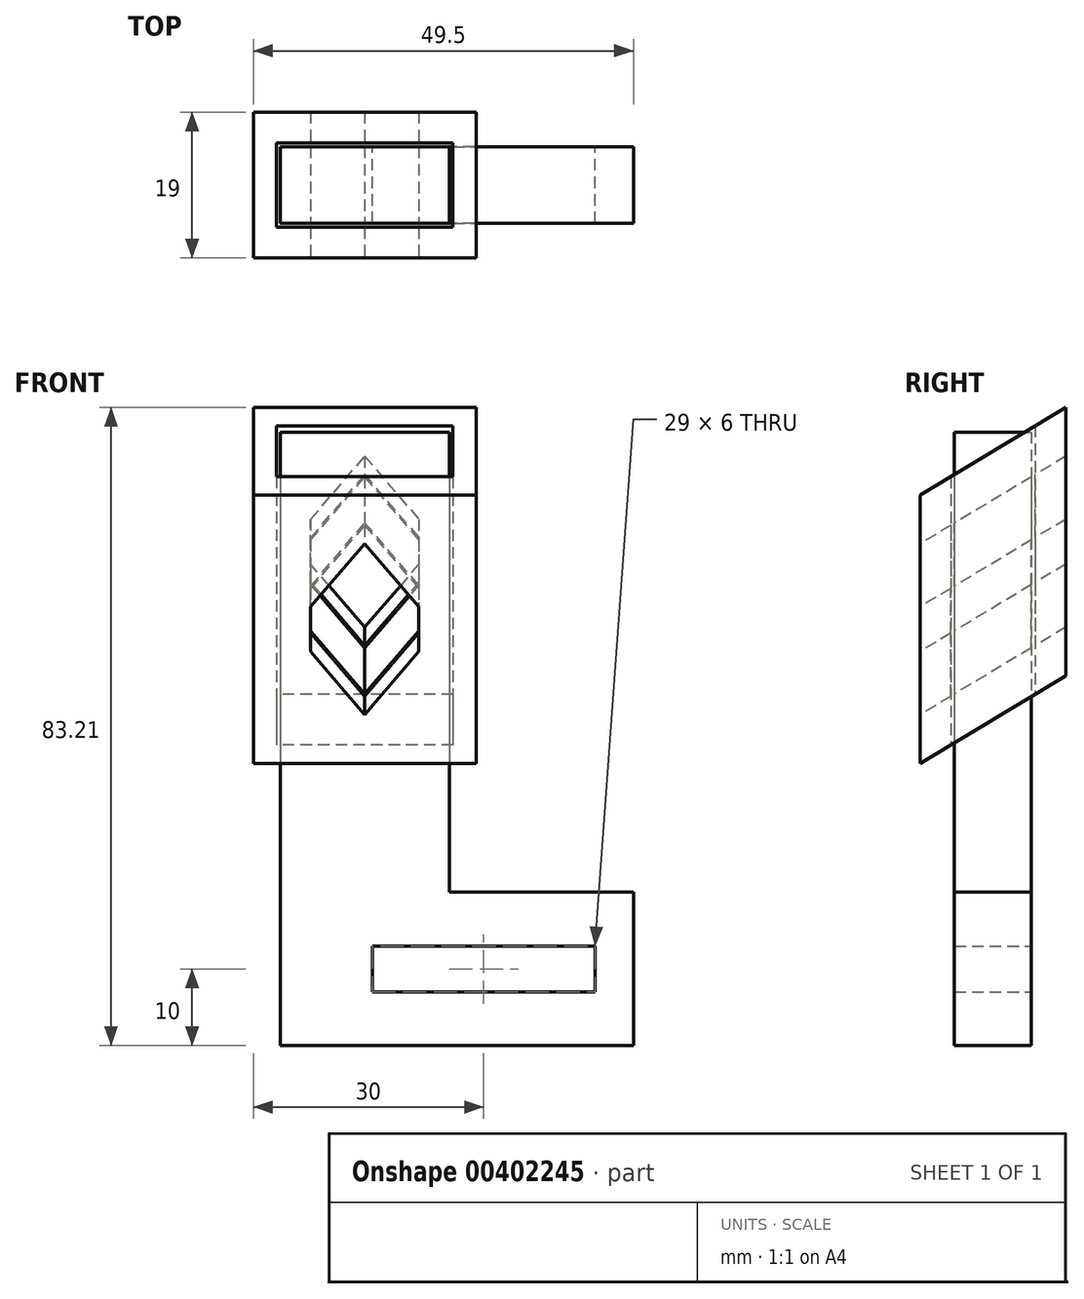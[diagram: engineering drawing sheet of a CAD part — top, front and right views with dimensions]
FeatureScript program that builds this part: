
annotation { "Feature Type Name" : "Feature", "Feature Type Description" : "" }
export const myFeature = defineFeature(function(context is Context, id is Id, definition is map)
    precondition{}
    {
        {
            var Q0;
            Q0=qCreatedBy(makeId("Top.planeOp"),FACE);
            var sketch = newSketch(context, id + "F0", { "sketchPlane" : qUnion([Q0])});
            skLineSegment(sketch, "E0.bottom", {"start": v(11, -5) * mm, "end": v(-11, -5) * mm});
            skLineSegment(sketch, "E0.top", {"start": v(11, 5) * mm, "end": v(-11, 5) * mm});
            skLineSegment(sketch, "E0.left", {"start": v(11, -5) * mm, "end": v(11, 5) * mm});
            skLineSegment(sketch, "E0.right", {"start": v(-11, -5) * mm, "end": v(-11, 5) * mm});
            skPoint(sketch, "E0.middle", {"position": v(0, 0) * mm});
            skLineSegment(sketch, "E1.bottom", {"start": v(11.5, 5.5) * mm, "end": v(-11.5, 5.5) * mm});
            skLineSegment(sketch, "E1.top", {"start": v(11.5, -5.5) * mm, "end": v(-11.5, -5.5) * mm});
            skLineSegment(sketch, "E1.left", {"start": v(11.5, 5.5) * mm, "end": v(11.5, -5.5) * mm});
            skLineSegment(sketch, "E1.right", {"start": v(-11.5, 5.5) * mm, "end": v(-11.5, -5.5) * mm});
            skLineSegment(sketch, "E2.bottom", {"start": v(14.5, 9.5) * mm, "end": v(-14.5, 9.5) * mm});
            skLineSegment(sketch, "E2.top", {"start": v(14.5, -9.5) * mm, "end": v(-14.5, -9.5) * mm});
            skLineSegment(sketch, "E2.left", {"start": v(14.5, 9.5) * mm, "end": v(14.5, -9.5) * mm});
            skLineSegment(sketch, "E2.right", {"start": v(-14.5, 9.5) * mm, "end": v(-14.5, -9.5) * mm});
            skSolve(sketch);
        }
        {
            var Q0;
            Q0=makeQuery(id+"F0.imprint","IMPRINT",FACE,{"disambiguationData":[TD([[makeQuery(id+"F0.imprint","IMPRINT",EDGE,{"derivedFrom":sQuery(id+"F0.wireOp",EDGE,"E0.bottom")}),-1.0]])]});
            extrude(context, id + "F1", {"entities" : qUnion([Q0]), "depth" : 70 * mm, "hasSecondDirection" : true, "secondDirectionOppositeDirection" : true, "secondDirectionDepth" : 10 * mm});
        }
        {
            var Q0;
            Q0=makeQuery(id+"F0.imprint","IMPRINT",FACE,{"disambiguationData":[TD([[makeQuery(id+"F0.imprint","IMPRINT",EDGE,{"derivedFrom":sQuery(id+"F0.wireOp",EDGE,"E1.bottom")}),-1.0]])]});
            extrude(context, id + "F2", {"entities" : qUnion([Q0]), "depth" : 80 * mm, "hasSecondDirection" : true, "secondDirectionOppositeDirection" : true, "secondDirectionDepth" : -20 * mm});
        }
        {
            var Q0;
            Q0=qCreatedBy(makeId("Front.planeOp"),FACE);
            var sketch = newSketch(context, id + "F3", { "sketchPlane" : qUnion([Q0])});
            skCircle(sketch, "E3.cCircle", {"center": v(0, 50) * mm, "radius": 6.75 * mm, "construction": true});
            skLineSegment(sketch, "E4", {"start": v(0, 59.55) * mm, "end": v(7.05, 52.5) * mm});
            skLineSegment(sketch, "E5", {"start": v(7.05, 52.5) * mm, "end": v(7.05, 47.5) * mm});
            skLineSegment(sketch, "E6", {"start": v(7.05, 47.5) * mm, "end": v(0, 40.45) * mm});
            skLineSegment(sketch, "E7", {"start": v(0, 40.45) * mm, "end": v(-7.05, 47.5) * mm});
            skLineSegment(sketch, "E8", {"start": v(-7.05, 47.5) * mm, "end": v(-7.05, 52.5) * mm});
            skLineSegment(sketch, "E9", {"start": v(-7.05, 52.5) * mm, "end": v(0, 59.55) * mm});
            skLineSegment(sketch, "E10", {"start": v(0, 50) * mm, "end": v(-27.01, 50) * mm, "construction": true});
            skPoint(sketch, "E10.endSnap0", {"position": v(-7.05, 50) * mm});
            skLineSegment(sketch, "E11.bottom", {"start": v(20, 65) * mm, "end": v(-20, 65) * mm});
            skLineSegment(sketch, "E11.top", {"start": v(20, 35) * mm, "end": v(-20, 35) * mm});
            skLineSegment(sketch, "E11.left", {"start": v(20, 65) * mm, "end": v(20, 35) * mm});
            skLineSegment(sketch, "E11.right", {"start": v(-20, 65) * mm, "end": v(-20, 35) * mm});
            skSolve(sketch);
        }
        {
            var Q0;
            Q0=makeQuery(id+"F3.imprint","IMPRINT",FACE,{"disambiguationData":[TD([[makeQuery(id+"F3.imprint","IMPRINT",EDGE,{"derivedFrom":sQuery(id+"F3.wireOp",EDGE,"E4")}),-1.0]])]});
            extrude(context, id + "F4", {"entities" : qUnion([Q0]), "endBound" : BoundingType.SYMMETRIC, "oppositeDirection" : true, "depth" : 50 * mm});
        }
        {
            var Q0;
            Q0=makeQuery(id+"F4.opExtrude","SWEPT_BODY",BODY,{"disambiguationData":[OSD([sQuery(id+"F3.wireOp",EDGE,"E4"),sQuery(id+"F3.wireOp",EDGE,"E5"),sQuery(id+"F3.wireOp",EDGE,"E6"),sQuery(id+"F3.wireOp",EDGE,"E7"),sQuery(id+"F3.wireOp",EDGE,"E8"),sQuery(id+"F3.wireOp",EDGE,"E9")])]});
            var Q1;
            Q1=sQuery(id+"F3.wireOp",EDGE,"E10");
            var Q2;
            Q2=sQuery(id+"F3.wireOp",EDGE,"E10");
            transform(context, id + "F5", {"entities" : qUnion([Q0]), "transformType" : TransformType.ROTATION, "transformAxis" : qUnion([Q2]), "angle" : 31 * degree, "oppositeDirection" : true, "makeCopy" : false});
        }
        {
            var Q0;
            Q0=makeQuery(id+"F4.opExtrude","SWEPT_BODY",BODY,{"disambiguationData":[OSD([sQuery(id+"F3.wireOp",EDGE,"E4"),sQuery(id+"F3.wireOp",EDGE,"E5"),sQuery(id+"F3.wireOp",EDGE,"E6"),sQuery(id+"F3.wireOp",EDGE,"E7"),sQuery(id+"F3.wireOp",EDGE,"E8"),sQuery(id+"F3.wireOp",EDGE,"E9")])]});
            var Q1;
            Q1=makeQuery(id+"F2.opExtrude","SWEPT_BODY",BODY,{"disambiguationData":[OSD([sQuery(id+"F0.wireOp",EDGE,"E1.bottom"),sQuery(id+"F0.wireOp",EDGE,"E1.top"),sQuery(id+"F0.wireOp",EDGE,"E1.left"),sQuery(id+"F0.wireOp",EDGE,"E1.right"),sQuery(id+"F0.wireOp",EDGE,"E2.bottom"),sQuery(id+"F0.wireOp",EDGE,"E2.top"),sQuery(id+"F0.wireOp",EDGE,"E2.left"),sQuery(id+"F0.wireOp",EDGE,"E2.right")])]});
            var Q2;
            Q2=makeQuery(id+"F1.opExtrude","SWEPT_BODY",BODY,{"disambiguationData":[OSD([sQuery(id+"F0.wireOp",EDGE,"E0.bottom"),sQuery(id+"F0.wireOp",EDGE,"E0.top"),sQuery(id+"F0.wireOp",EDGE,"E0.left"),sQuery(id+"F0.wireOp",EDGE,"E0.right")])]});
            booleanBodies(context, id + "F6", {"operationType" : BooleanOperationType.SUBTRACTION, "tools" : qUnion([Q0]), "targets" : qUnion([Q1, Q2])});
        }
        {
            var Q0;
            Q0=makeQuery(id+"F3.imprint","IMPRINT",FACE,{"disambiguationData":[TD([[makeQuery(id+"F3.imprint","IMPRINT",EDGE,{"derivedFrom":sQuery(id+"F3.wireOp",EDGE,"E4")}),1.0]])]});
            var Q1;
            Q1=makeQuery(id+"F3.imprint","IMPRINT",FACE,{"disambiguationData":[TD([[makeQuery(id+"F3.imprint","IMPRINT",EDGE,{"derivedFrom":sQuery(id+"F3.wireOp",EDGE,"E4")}),-1.0]])]});
            extrude(context, id + "F7", {"entities" : qUnion([Q0, Q1]), "endBound" : BoundingType.SYMMETRIC, "depth" : 50 * mm});
        }
        {
            var Q0;
            Q0=makeQuery(id+"F7.opExtrude","SWEPT_BODY",BODY,{"disambiguationData":[OSD([sQuery(id+"F3.wireOp",EDGE,"E11.bottom"),sQuery(id+"F3.wireOp",EDGE,"E11.top"),sQuery(id+"F3.wireOp",EDGE,"E11.left"),sQuery(id+"F3.wireOp",EDGE,"E11.right")])]});
            var Q1;
            Q1=sQuery(id+"F3.wireOp",EDGE,"E10");
            transform(context, id + "F8", {"entities" : qUnion([Q0]), "transformType" : TransformType.ROTATION, "transformAxis" : qUnion([Q1]), "angle" : 31 * degree, "oppositeDirection" : true, "makeCopy" : false});
        }
        {
            var Q0;
            Q0=makeQuery(id+"F7.opExtrude","SWEPT_BODY",BODY,{"disambiguationData":[OSD([sQuery(id+"F3.wireOp",EDGE,"E11.bottom"),sQuery(id+"F3.wireOp",EDGE,"E11.top"),sQuery(id+"F3.wireOp",EDGE,"E11.left"),sQuery(id+"F3.wireOp",EDGE,"E11.right")])]});
            var Q1;
            Q1=makeQuery(id+"F2.opExtrude","SWEPT_BODY",BODY,{"disambiguationData":[OSD([sQuery(id+"F0.wireOp",EDGE,"E1.bottom"),sQuery(id+"F0.wireOp",EDGE,"E1.top"),sQuery(id+"F0.wireOp",EDGE,"E1.left"),sQuery(id+"F0.wireOp",EDGE,"E1.right"),sQuery(id+"F0.wireOp",EDGE,"E2.bottom"),sQuery(id+"F0.wireOp",EDGE,"E2.top"),sQuery(id+"F0.wireOp",EDGE,"E2.left"),sQuery(id+"F0.wireOp",EDGE,"E2.right")])]});
            booleanBodies(context, id + "F9", {"operationType" : BooleanOperationType.INTERSECTION, "tools" : qUnion([Q0, Q1])});
        }
        {
            var Q0;
            Q0=qCreatedBy(makeId("Front.planeOp"),FACE);
            var sketch = newSketch(context, id + "F10", { "sketchPlane" : qUnion([Q0])});
            skLineSegment(sketch, "E12.bottom", {"start": v(11, 10) * mm, "end": v(35, 10) * mm});
            skLineSegment(sketch, "E12.top", {"start": v(11, -10) * mm, "end": v(35, -10) * mm});
            skLineSegment(sketch, "E12.left", {"start": v(11, 10) * mm, "end": v(11, -10) * mm});
            skLineSegment(sketch, "E12.right", {"start": v(35, 10) * mm, "end": v(35, -10) * mm});
            skPoint(sketch, "E12.middle", {"position": v(23, 0) * mm});
            skSolve(sketch);
        }
        {
            var Q0;
            Q0 = qSketchRegion(id + "F10", true);
            extrude(context, id + "F11", {"entities" : qUnion([Q0]), "operationType" : NewBodyOperationType.ADD, "endBound" : BoundingType.SYMMETRIC, "depth" : 10 * mm, "hasSecondDirection" : true, "secondDirectionOppositeDirection" : false, "secondDirectionDepth" : 1 * mm});
        }
        {
            var Q0;
            Q0=makeQuery(id+"F11.boolean.opBoolean","MERGE",FACE,{"derivedFrom":[makeQuery(id+"F1.opExtrude","SWEPT_FACE",FACE,{"disambiguationData":[OSD([sQuery(id+"F0.wireOp",EDGE,"E0.top")])]}),makeQuery(id+"F11.opExtrude","CAP_FACE",FACE,{"disambiguationData":[OSD([sQuery(id+"F10.wireOp",EDGE,"E12.bottom"),sQuery(id+"F10.wireOp",EDGE,"E12.top"),sQuery(id+"F10.wireOp",EDGE,"E12.left"),sQuery(id+"F10.wireOp",EDGE,"E12.right")])],"isStart":true})]});
            var sketch = newSketch(context, id + "F12", { "sketchPlane" : qUnion([Q0])});
            skLineSegment(sketch, "E13.bottom", {"start": v(-1, 3) * mm, "end": v(-30, 3) * mm});
            skLineSegment(sketch, "E13.top", {"start": v(-1, -3) * mm, "end": v(-30, -3) * mm});
            skLineSegment(sketch, "E13.left", {"start": v(-1, 3) * mm, "end": v(-1, -3) * mm});
            skLineSegment(sketch, "E13.right", {"start": v(-30, 3) * mm, "end": v(-30, -3) * mm});
            skPoint(sketch, "E13.middle", {"position": v(-15.5, 0) * mm});
            skSolve(sketch);
        }
        {
            var Q0;
            Q0 = qSketchRegion(id + "F12", true);
            extrude(context, id + "F13", {"entities" : qUnion([Q0]), "operationType" : NewBodyOperationType.REMOVE, "oppositeDirection" : true, "depth" : 25 * mm});
        }
    });
